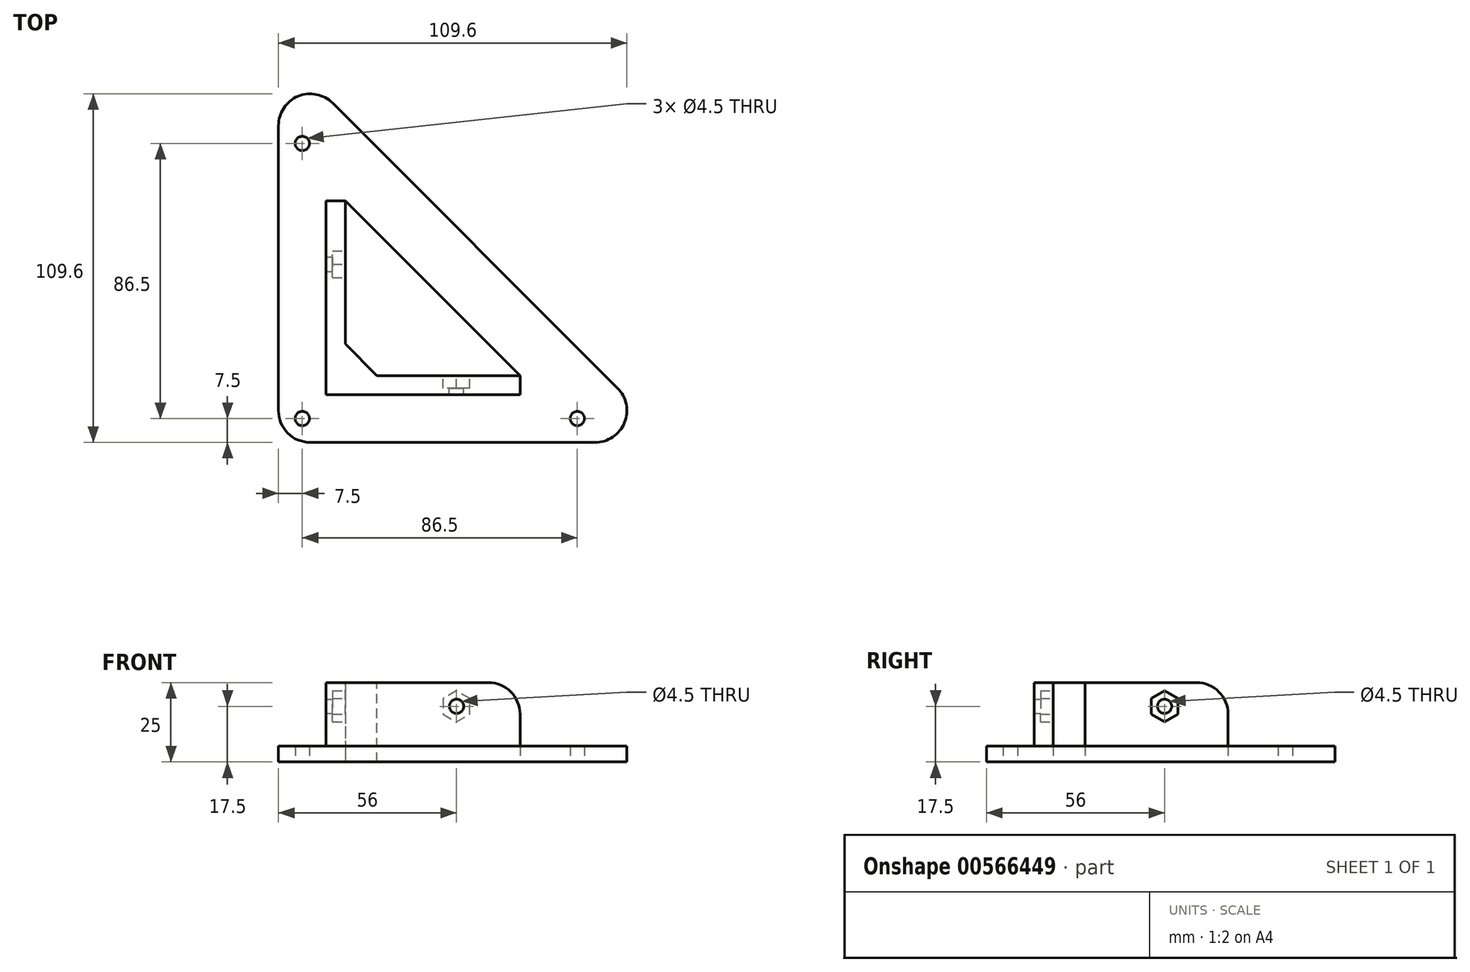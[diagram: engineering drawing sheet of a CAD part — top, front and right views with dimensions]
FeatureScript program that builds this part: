
annotation { "Feature Type Name" : "Feature", "Feature Type Description" : "" }
export const myFeature = defineFeature(function(context is Context, id is Id, definition is map)
    precondition{}
    {
        {
            var Q0;
            Q0=qCreatedBy(makeId("Top.planeOp"),FACE);
            var sketch = newSketch(context, id + "F0", { "sketchPlane" : qUnion([Q0])});
            skLineSegment(sketch, "E0", {"start": v(0, 123.74) * mm, "end": v(123.74, 0) * mm});
            skLineSegment(sketch, "E1", {"start": v(123.74, 0) * mm, "end": v(103.74, 0) * mm});
            skLineSegment(sketch, "E2", {"start": v(103.74, 0) * mm, "end": v(0, 103.74) * mm, "construction": true});
            skLineSegment(sketch, "E3", {"start": v(0, 103.74) * mm, "end": v(0, 123.74) * mm});
            skLineSegment(sketch, "E4", {"start": v(0, 103.74) * mm, "end": v(0, 0) * mm});
            skLineSegment(sketch, "E5", {"start": v(0, 0) * mm, "end": v(103.74, 0) * mm});
            skLineSegment(sketch, "E6", {"start": v(21, 76) * mm, "end": v(21, 21) * mm});
            skLineSegment(sketch, "E7", {"start": v(21, 21) * mm, "end": v(76, 21) * mm});
            skLineSegment(sketch, "E8", {"start": v(76, 21) * mm, "end": v(21, 76) * mm});
            skCircle(sketch, "E9", {"center": v(7.5, 94) * mm, "radius": 2.25 * mm});
            skCircle(sketch, "E10", {"center": v(94, 7.5) * mm, "radius": 2.25 * mm});
            skCircle(sketch, "E11", {"center": v(7.5, 7.5) * mm, "radius": 2.25 * mm});
            skSolve(sketch);
        }
        {
            var Q0;
            Q0=qSketchRegion(id+"F0",true);
            extrude(context, id + "F1", {"entities" : qUnion([Q0]), "depth" : 5 * mm, "offsetDistance" : 25 * mm});
        }
        {
            var Q0;
            Q0=makeQuery(id+"F1.opExtrude","CAP_FACE",FACE,{"disambiguationData":[OSD([sQuery(id+"F0.wireOp",EDGE,"E0"),sQuery(id+"F0.wireOp",EDGE,"E1"),sQuery(id+"F0.wireOp",EDGE,"E3"),sQuery(id+"F0.wireOp",EDGE,"E4"),sQuery(id+"F0.wireOp",EDGE,"E5"),sQuery(id+"F0.wireOp",EDGE,"E6"),sQuery(id+"F0.wireOp",EDGE,"E7"),sQuery(id+"F0.wireOp",EDGE,"E8")])],"isStart":false});
            var sketch = newSketch(context, id + "F2", { "sketchPlane" : qUnion([Q0])});
            skLineSegment(sketch, "E12", {"start": v(76, 21) * mm, "end": v(21, 21) * mm});
            skLineSegment(sketch, "E13", {"start": v(15, 15) * mm, "end": v(76, 15) * mm});
            skLineSegment(sketch, "E14", {"start": v(76, 15) * mm, "end": v(76, 21) * mm});
            skLineSegment(sketch, "E15", {"start": v(21, 76) * mm, "end": v(21, 21) * mm});
            skLineSegment(sketch, "E16", {"start": v(15, 15) * mm, "end": v(15, 76) * mm});
            skLineSegment(sketch, "E17", {"start": v(15, 76) * mm, "end": v(21, 76) * mm});
            skLineSegment(sketch, "E18", {"start": v(15, 15) * mm, "end": v(15, 15) * mm});
            skPoint(sketch, "E18.endSnap0", {"position": v(15, 45.5) * mm});
            skSolve(sketch);
        }
        {
            var Q0;
            Q0=qSketchRegion(id+"F2",true);
            extrude(context, id + "F3", {"entities" : qUnion([Q0]), "operationType" : NewBodyOperationType.ADD, "depth" : 20 * mm, "offsetDistance" : 25 * mm});
        }
        {
            var Q0;
            Q0=makeQuery(id+"F1.opExtrude","SWEPT_EDGE",EDGE,{"disambiguationData":[OSD([sQuery(id+"F0.wireOp",EDGE,"E0"),sQuery(id+"F0.wireOp",EDGE,"E3")])]});
            var Q1;
            Q1=makeQuery(id+"F1.opExtrude","SWEPT_EDGE",EDGE,{"disambiguationData":[OSD([sQuery(id+"F0.wireOp",EDGE,"E0"),sQuery(id+"F0.wireOp",EDGE,"E1")])]});
            var Q2;
            Q2=makeQuery(id+"F3.opExtrude","CAP_EDGE",EDGE,{"disambiguationData":[OSD([sQuery(id+"F2.wireOp",EDGE,"E14")])],"isStart":false});
            var Q3;
            Q3=makeQuery(id+"F3.opExtrude","CAP_EDGE",EDGE,{"disambiguationData":[OSD([sQuery(id+"F2.wireOp",EDGE,"E17")])],"isStart":false});
            var Q4;
            Q4=makeQuery(id+"F1.opExtrude","SWEPT_EDGE",EDGE,{"disambiguationData":[OSD([sQuery(id+"F0.wireOp",EDGE,"E4"),sQuery(id+"F0.wireOp",EDGE,"E5")])]});
            fillet(context, id + "F4", {"entities" : qUnion([Q0, Q1, Q2, Q3, Q4]), "radius" : 10 * mm, "tangentPropagation" : true, "allowEdgeOverflow" : false});
        }
        {
            var Q0;
            Q0=makeQuery(id+"F3.boolean.opBoolean","MERGE",FACE,{"derivedFrom":[makeQuery(id+"F1.opExtrude","SWEPT_FACE",FACE,{"disambiguationData":[OSD([sQuery(id+"F0.wireOp",EDGE,"E6")])]}),makeQuery(id+"F3.opExtrude","SWEPT_FACE",FACE,{"disambiguationData":[OSD([sQuery(id+"F2.wireOp",EDGE,"E15")])]})]});
            var sketch = newSketch(context, id + "F5", { "sketchPlane" : qUnion([Q0])});
            skCircle(sketch, "E19", {"center": v(56, 17.5) * mm, "radius": 2.25 * mm});
            skSolve(sketch);
        }
        {
            var Q0;
            Q0=qSketchRegion(id+"F5",true);
            extrude(context, id + "F6", {"entities" : qUnion([Q0]), "operationType" : NewBodyOperationType.REMOVE, "oppositeDirection" : true, "depth" : 25 * mm, "offsetDistance" : 25 * mm});
        }
        {
            var Q0;
            Q0=makeQuery(id+"F3.boolean.opBoolean","MERGE",FACE,{"derivedFrom":[makeQuery(id+"F1.opExtrude","SWEPT_FACE",FACE,{"disambiguationData":[OSD([sQuery(id+"F0.wireOp",EDGE,"E7")])]}),makeQuery(id+"F3.opExtrude","SWEPT_FACE",FACE,{"disambiguationData":[OSD([sQuery(id+"F2.wireOp",EDGE,"E12")])]})]});
            var sketch = newSketch(context, id + "F7", { "sketchPlane" : qUnion([Q0])});
            skCircle(sketch, "E20", {"center": v(-56, 17.5) * mm, "radius": 2.25 * mm});
            skSolve(sketch);
        }
        {
            var Q0;
            Q0=qSketchRegion(id+"F7",true);
            extrude(context, id + "F8", {"entities" : qUnion([Q0]), "operationType" : NewBodyOperationType.REMOVE, "oppositeDirection" : true, "depth" : 25 * mm, "offsetDistance" : 25 * mm});
        }
        {
            var Q0;
            Q0=makeQuery(id+"F3.opExtrude","CAP_EDGE",EDGE,{"disambiguationData":[OSD([sQuery(id+"F2.wireOp",EDGE,"E17")])],"isStart":true});
            var Q1;
            Q1=makeQuery(id+"F3.opExtrude","CAP_EDGE",EDGE,{"disambiguationData":[OSD([sQuery(id+"F2.wireOp",EDGE,"E14")])],"isStart":true});
            var Q2;
            Q2=makeQuery(id+"F3.boolean.opBoolean","MERGE",EDGE,{"derivedFrom":[makeQuery(id+"F1.opExtrude","SWEPT_EDGE",EDGE,{"disambiguationData":[OSD([sQuery(id+"F0.wireOp",EDGE,"E6"),sQuery(id+"F0.wireOp",EDGE,"E7")])]}),makeQuery(id+"F3.opExtrude","SWEPT_EDGE",EDGE,{"disambiguationData":[OSD([sQuery(id+"F2.wireOp",EDGE,"E12"),sQuery(id+"F2.wireOp",EDGE,"E15")])]})]});
            chamfer(context, id + "F9", {"entities" : qUnion([Q0, Q1, Q2]), "width" : 10 * mm, "tangentPropagation" : true});
        }
        {
            var Q0;
            Q0=makeQuery(id+"F3.boolean.opBoolean","MERGE",FACE,{"derivedFrom":[makeQuery(id+"F1.opExtrude","SWEPT_FACE",FACE,{"disambiguationData":[OSD([sQuery(id+"F0.wireOp",EDGE,"E7")])]}),makeQuery(id+"F3.opExtrude","SWEPT_FACE",FACE,{"disambiguationData":[OSD([sQuery(id+"F2.wireOp",EDGE,"E12")])]})]});
            var sketch = newSketch(context, id + "F10", { "sketchPlane" : qUnion([Q0])});
            skCircle(sketch, "E21.cCircle", {"center": v(-56, 17.5) * mm, "radius": 4.22 * mm, "construction": true});
            skLineSegment(sketch, "E21.0", {"start": v(-51.78, 19.94) * mm, "end": v(-51.78, 15.06) * mm});
            skLineSegment(sketch, "E21.1", {"start": v(-51.78, 15.06) * mm, "end": v(-56, 12.62) * mm});
            skLineSegment(sketch, "E21.2", {"start": v(-56, 12.62) * mm, "end": v(-60.23, 15.06) * mm});
            skLineSegment(sketch, "E21.3", {"start": v(-60.23, 15.06) * mm, "end": v(-60.23, 19.94) * mm});
            skLineSegment(sketch, "E21.4", {"start": v(-60.23, 19.94) * mm, "end": v(-56, 22.38) * mm});
            skLineSegment(sketch, "E21.5", {"start": v(-56, 22.38) * mm, "end": v(-51.78, 19.94) * mm});
            skPoint(sketch, "E21.0.midPoint", {"position": v(-51.78, 17.5) * mm});
            skSolve(sketch);
        }
        {
            var Q0;
            Q0=qSketchRegion(id+"F10",true);
            extrude(context, id + "F11", {"entities" : qUnion([Q0]), "operationType" : NewBodyOperationType.REMOVE, "oppositeDirection" : true, "depth" : 4 * mm, "offsetDistance" : 25 * mm});
        }
        {
            var Q0;
            Q0=makeQuery(id+"F3.boolean.opBoolean","MERGE",FACE,{"derivedFrom":[makeQuery(id+"F1.opExtrude","SWEPT_FACE",FACE,{"disambiguationData":[OSD([sQuery(id+"F0.wireOp",EDGE,"E6")])]}),makeQuery(id+"F3.opExtrude","SWEPT_FACE",FACE,{"disambiguationData":[OSD([sQuery(id+"F2.wireOp",EDGE,"E15")])]})]});
            var sketch = newSketch(context, id + "F12", { "sketchPlane" : qUnion([Q0])});
            skCircle(sketch, "E22.cCircle", {"center": v(56, 17.5) * mm, "radius": 4.22 * mm, "construction": true});
            skLineSegment(sketch, "E22.0", {"start": v(60.22, 19.94) * mm, "end": v(60.22, 15.06) * mm});
            skLineSegment(sketch, "E22.1", {"start": v(60.22, 15.06) * mm, "end": v(56, 12.62) * mm});
            skLineSegment(sketch, "E22.2", {"start": v(56, 12.62) * mm, "end": v(51.77, 15.06) * mm});
            skLineSegment(sketch, "E22.3", {"start": v(51.77, 15.06) * mm, "end": v(51.77, 19.94) * mm});
            skLineSegment(sketch, "E22.4", {"start": v(51.77, 19.94) * mm, "end": v(56, 22.38) * mm});
            skLineSegment(sketch, "E22.5", {"start": v(56, 22.38) * mm, "end": v(60.22, 19.94) * mm});
            skPoint(sketch, "E22.0.midPoint", {"position": v(60.22, 17.5) * mm});
            skSolve(sketch);
        }
        {
            var Q0;
            Q0=qSketchRegion(id+"F12",true);
            extrude(context, id + "F13", {"entities" : qUnion([Q0]), "operationType" : NewBodyOperationType.REMOVE, "oppositeDirection" : true, "depth" : 4 * mm, "offsetDistance" : 25 * mm});
        }
    });
